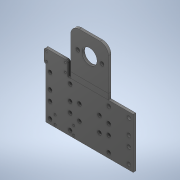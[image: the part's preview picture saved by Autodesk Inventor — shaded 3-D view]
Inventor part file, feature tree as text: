
AUTODESK INVENTOR PART (.ipt)
format: ipt  version: 2020 (Build 240168000, 168)  size: 288,256 bytes
history: native  units: mm
features: sheet_metal_op x9, other x9, sketch x8, fillet x2, pattern_linear x1, mirror x1
ambient origin geometry x8: Origin, YZ Plane, XZ Plane, XY Plane, X Axis, Y Axis, Z Axis, Center Point
bodies: Solid1 (feature_tree)
feature tree (30):
  sheet_metal_op  "Face1"
  pattern_linear  "Rectangular Pattern1"  Count1=6  [1 undecoded]
  mirror  "Mirror1"
  sheet_metal_op  "Face2"
  sheet_metal_op  "Flange1"
  fillet  "Fillet2"  Radius=3.0mm
  sheet_metal_op  "Face3"
  fillet  "Fillet3"  Radius=5.0mm
  sheet_metal_op  "Unfold1"
  sketch  "Sketch1"  dims[d1=104.0mm d2=60.0mm d3=3.0mm]
  other  "Plate1"
  sketch  "Sketch2"  dims[d4=24.0mm d5=18.0mm d8=4.5mm d9=4.5mm d10=4.5mm d11=4.5mm d12=5.0mm]
  sketch  "Sketch3"  dims[d13=15.0mm]
  sketch  "Sketch4"  dims[d14=3.0mm]
  other  "Plate2"
  sheet_metal_op  "Bend1"
  sketch  "Sketch5"  dims[d15=0.0mm]
  other  "Plate3"
  sheet_metal_op  "Bend2"
  sheet_metal_op  "Corner1"
  sketch  "Sketch6"  dims[d16=20.0mm d18=30.0mm]
  other  "Plate4"
  sheet_metal_op  "Bend3"
  sketch  "Sketch9"  dims[d20=24.0mm d21=18.0mm d22=4.5mm d23=4.5mm d24=4.5mm d25=4.5mm]
  sketch  "Sketch10"  dims[d26=12.0mm d27=9.0mm d28=3.0mm d29=0.0mm d30=45.0mm d31=3.0mm d32=22.5mm d33=3.0mm d34=3.0mm d35=1.5mm d36=6.0mm d37=3.0mm d38=3.0mm d39=1.5mm d40=6.0mm d41=3.0mm d42=55.0mm d43=90.0deg d44=3.0mm d45=12.0mm d46=3.0mm d47=3.0mm d48=18.0mm d49=33.0mm d50=4.5mm d51=4.5mm d52=29.0mm d53=22.5mm d54=15.0mm d55=33.0mm d56=33.0mm d57=3.0mm d58=0.0mm d59=10.0mm d60=0.0mm d61=3.0mm d62=3.0mm d63=1.5mm d64=6.0mm d65=3.0mm d67=28.2mm d75=2.0mm d76=16.3mm d81=22.2mm d82=10.2mm d83=3.0mm d84=3.0mm d85=2.5mm d86=2.5mm d87=2.5mm d88=2.5mm d89=3.0mm d90=0.0mm d91=2.0mm d92=22.2mm d93=10.2mm d94=3.0mm d95=11.0mm d96=2.5mm d97=2.5mm d98=2.5mm d99=2.5mm d100=3.0mm d101=0.0mm]
  other  "Cut1"
  other  "Cut2"
  other  "Cut3"
  other  "Cut4"
  other  "Cut5"
note: 1 required parameter value undecoded (feature->parameter linkage not recoverable at this tier; creation-order binding heuristic only, values carry confidence <= 0.55)
